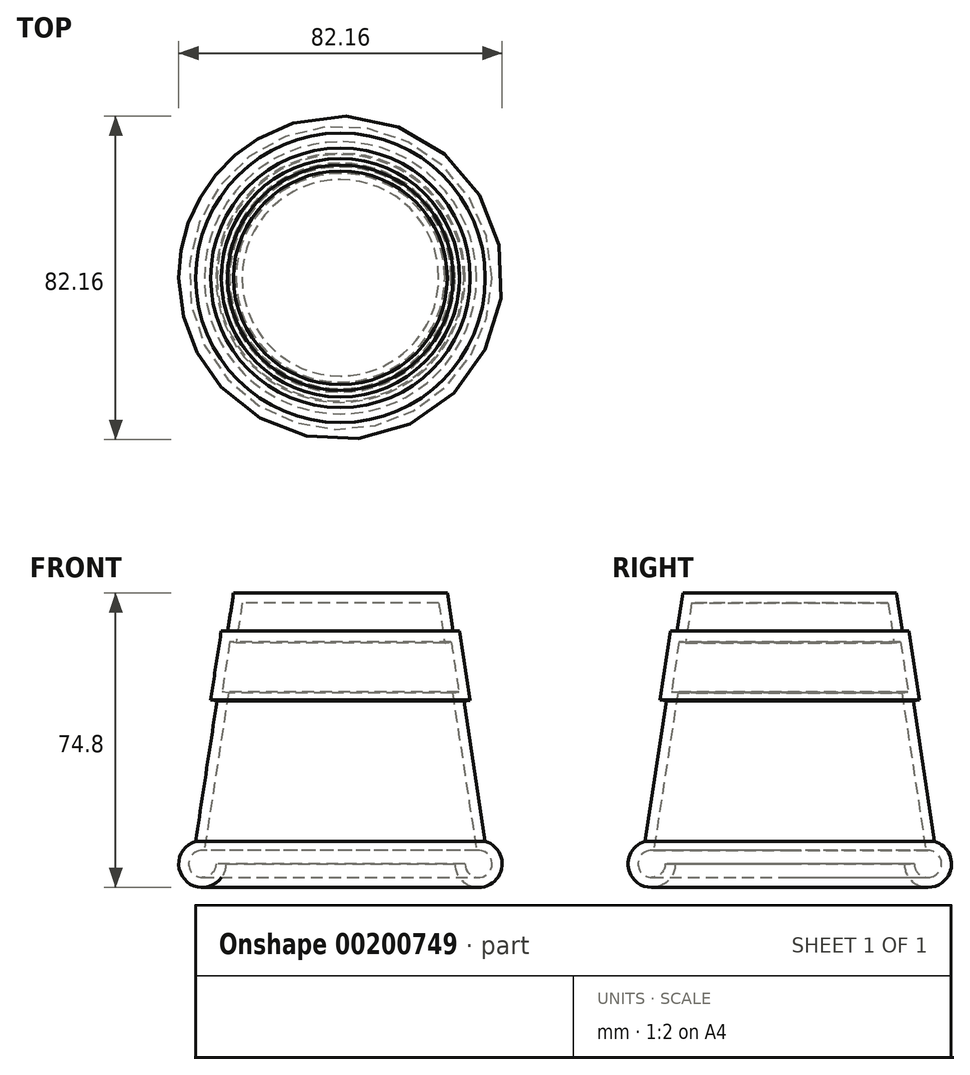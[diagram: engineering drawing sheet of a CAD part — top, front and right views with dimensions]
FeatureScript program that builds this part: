
annotation { "Feature Type Name" : "Feature", "Feature Type Description" : "" }
export const myFeature = defineFeature(function(context is Context, id is Id, definition is map)
    precondition{}
    {
        {
            var Q0;
            Q0=qCreatedBy(makeId("Front.planeOp"),FACE);
            var sketch = newSketch(context, id + "F0", { "sketchPlane" : qUnion([Q0])});
            skLineSegment(sketch, "E0", {"start": v(0, 0) * mm, "end": v(31.65, 0) * mm});
            skLineSegment(sketch, "E1", {"start": v(34.57, 3.4) * mm, "end": v(28.45, 43.47) * mm});
            skLineSegment(sketch, "E2", {"start": v(24.97, 66.28) * mm, "end": v(0, 66.28) * mm});
            skLineSegment(sketch, "E3", {"start": v(0, 66.28) * mm, "end": v(0, 0) * mm});
            skArc(sketch, "E4", {"start": v(31.65, 0) * mm, "mid": v(37.7, -2.24) * mm, "end": v(34.57, 3.4) * mm});
            skLineSegment(sketch, "E5", {"start": v(26.51, 56.17) * mm, "end": v(28.14, 56.38) * mm});
            skLineSegment(sketch, "E6", {"start": v(28.14, 56.38) * mm, "end": v(30.08, 43.72) * mm});
            skLineSegment(sketch, "E7", {"start": v(30.08, 43.72) * mm, "end": v(28.45, 43.47) * mm});
            skLineSegment(sketch, "E8.trimOffspring", {"start": v(26.51, 56.17) * mm, "end": v(24.97, 66.28) * mm});
            skSolve(sketch);
        }
        {
            var Q0;
            Q0=makeQuery(id+"F0.imprint","IMPRINT",FACE,{"disambiguationData":[TD([[makeQuery(id+"F0.imprint","IMPRINT",EDGE,{"derivedFrom":sQuery(id+"F0.wireOp",EDGE,"E0")}),1.0]])]});
            var Q1;
            Q1=sQuery(id+"F0.wireOp",EDGE,"E3");
            revolve(context, id + "F1", {"entities" : qUnion([Q0]), "axis" : qUnion([Q1]), "revolveType" : RevolveType.FULL});
        }
        {
            var Q0;
            Q0=makeQuery(id+"F1.opRevolve","SWEPT_FACE",FACE,{"disambiguationData":[OSD([sQuery(id+"F0.wireOp",EDGE,"E0")])]});
            shell(context, id + "F2", {"entities" : qUnion([Q0]), "thickness" : 2.54 * mm, "oppositeDirection" : true});
        }
    });
